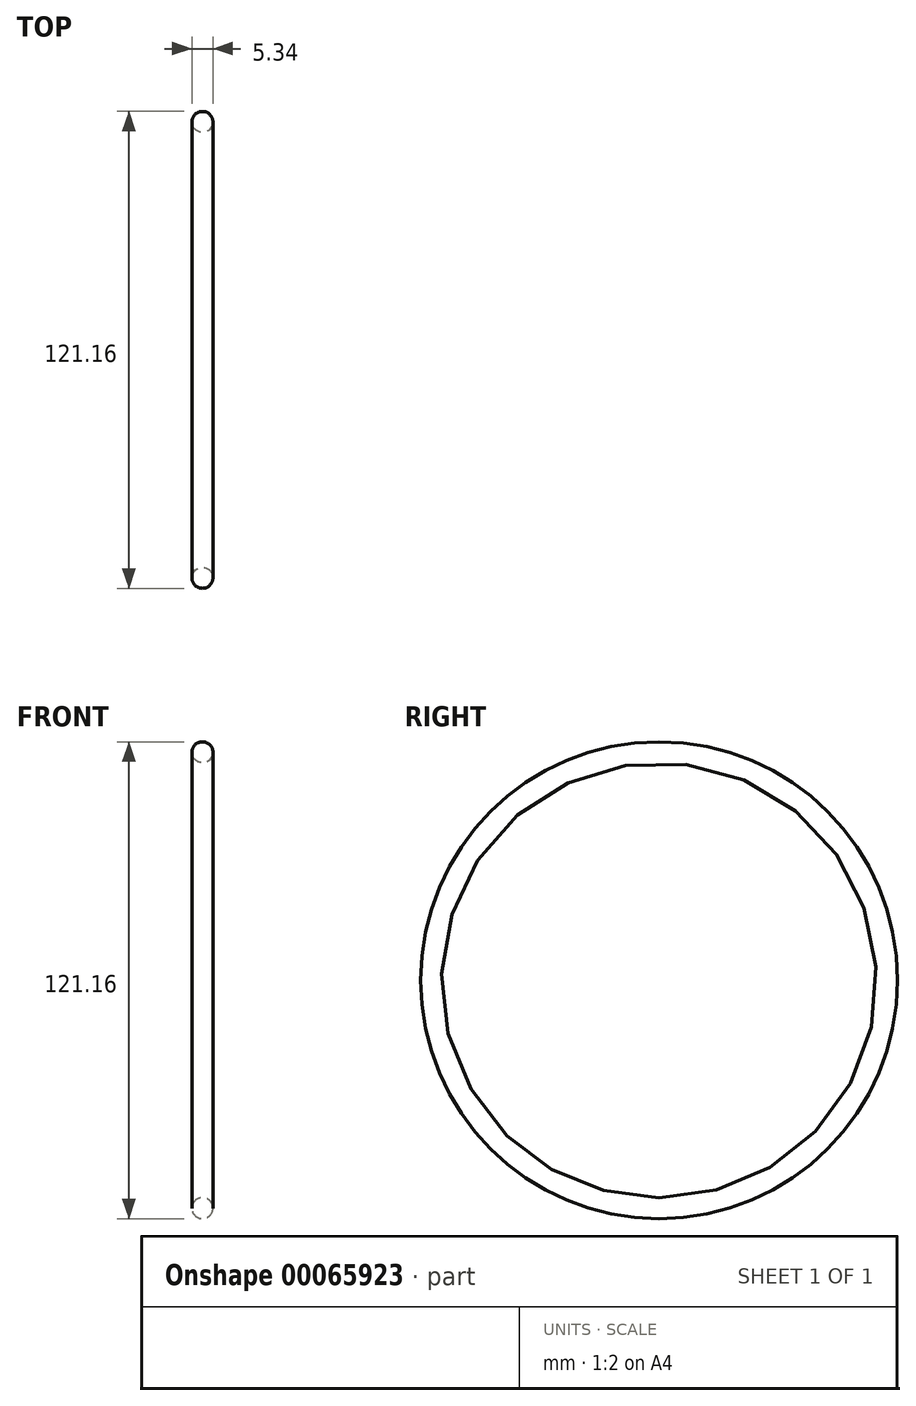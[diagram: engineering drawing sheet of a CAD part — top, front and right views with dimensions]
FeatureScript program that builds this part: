
annotation { "Feature Type Name" : "Feature", "Feature Type Description" : "" }
export const myFeature = defineFeature(function(context is Context, id is Id, definition is map)
    precondition{}
    {
        {
            var Q0;
            Q0=qCreatedBy(makeId("Front.planeOp"),FACE);
            var sketch = newSketch(context, id + "F0", { "sketchPlane" : qUnion([Q0])});
            skLineSegment(sketch, "E0", {"start": v(0, 0) * mm, "end": v(-6.06, 0) * mm, "construction": true});
            skCircle(sketch, "E1", {"center": v(0, 57.91) * mm, "radius": 2.67 * mm});
            skSolve(sketch);
        }
        {
            var Q0;
            Q0=makeQuery(id+"F0.imprint","IMPRINT",FACE,{"disambiguationData":[TD([[makeQuery(id+"F0.imprint","IMPRINT",EDGE,{"derivedFrom":sQuery(id+"F0.wireOp",EDGE,"E1")}),1.0]])]});
            var Q1;
            Q1=sQuery(id+"F0.wireOp",EDGE,"E0");
            revolve(context, id + "F1", {"entities" : qUnion([Q0]), "axis" : qUnion([Q1]), "revolveType" : RevolveType.FULL});
        }
    });
